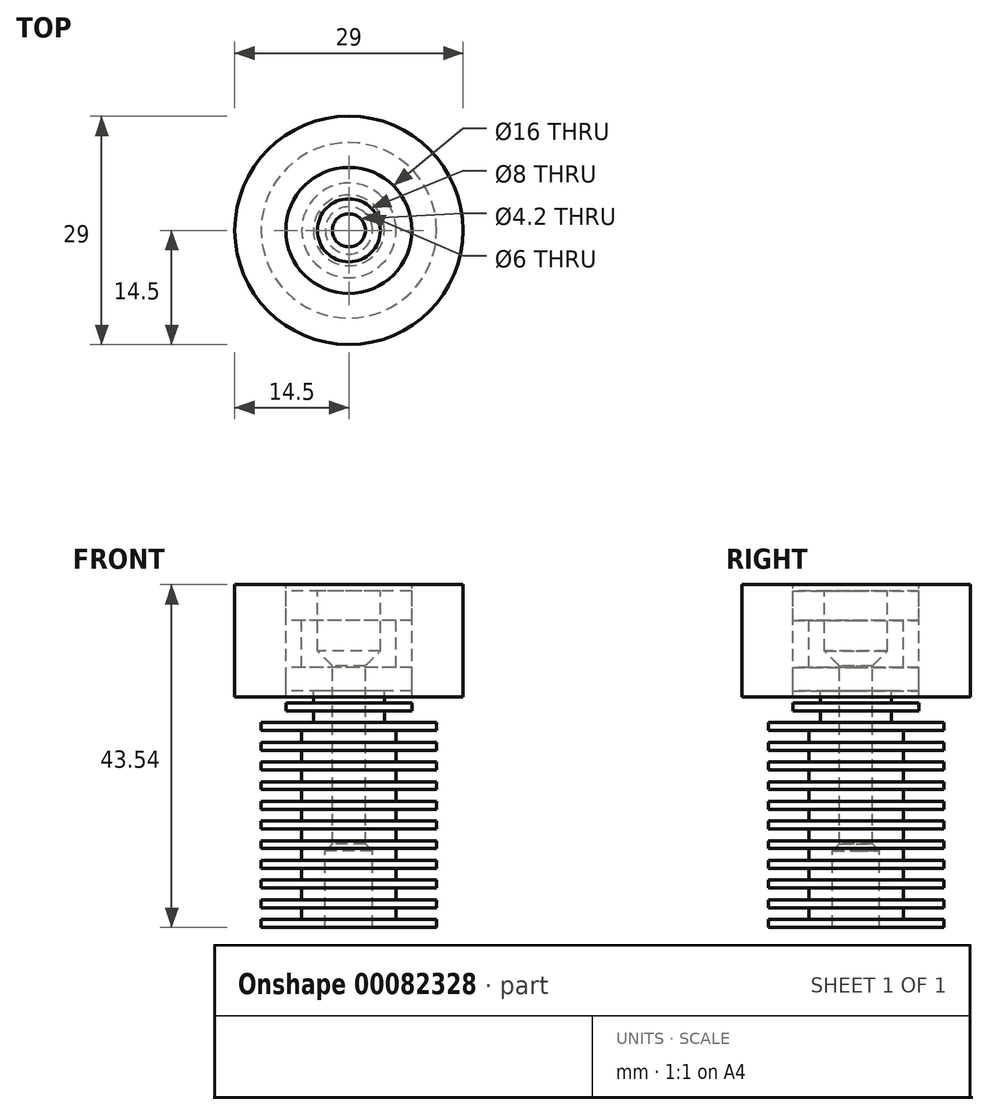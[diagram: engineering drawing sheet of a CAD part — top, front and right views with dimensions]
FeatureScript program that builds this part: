
annotation { "Feature Type Name" : "Feature", "Feature Type Description" : "" }
export const myFeature = defineFeature(function(context is Context, id is Id, definition is map)
    precondition{}
    {
        {
            var Q0;
            Q0=qCreatedBy(makeId("Front.planeOp"),FACE);
            var sketch = newSketch(context, id + "F0", { "sketchPlane" : qUnion([Q0])});
            skLineSegment(sketch, "E0", {"start": v(-11.15, 0) * mm, "end": v(-11.15, 1) * mm});
            skLineSegment(sketch, "E1", {"start": v(-11.15, 1) * mm, "end": v(-6, 1) * mm});
            skLineSegment(sketch, "E2", {"start": v(-6, 1) * mm, "end": v(-6, 2.5) * mm});
            skLineSegment(sketch, "E3", {"start": v(-6, 2.5) * mm, "end": v(-11.15, 2.5) * mm});
            skLineSegment(sketch, "E4.0.1.0", {"start": v(-11.15, 2.5) * mm, "end": v(-11.15, 3.5) * mm});
            skLineSegment(sketch, "E4.0.1.1", {"start": v(-11.15, 3.5) * mm, "end": v(-6, 3.5) * mm});
            skLineSegment(sketch, "E4.0.1.2", {"start": v(-6, 3.5) * mm, "end": v(-6, 5) * mm});
            skLineSegment(sketch, "E4.0.1.3", {"start": v(-6, 5) * mm, "end": v(-11.15, 5) * mm});
            skLineSegment(sketch, "E4.0.2.0", {"start": v(-11.15, 5) * mm, "end": v(-11.15, 6) * mm});
            skLineSegment(sketch, "E4.0.2.1", {"start": v(-11.15, 6) * mm, "end": v(-6, 6) * mm});
            skLineSegment(sketch, "E4.0.2.2", {"start": v(-6, 6) * mm, "end": v(-6, 7.5) * mm});
            skLineSegment(sketch, "E4.0.2.3", {"start": v(-6, 7.5) * mm, "end": v(-11.15, 7.5) * mm});
            skLineSegment(sketch, "E4.0.3.0", {"start": v(-11.15, 7.5) * mm, "end": v(-11.15, 8.5) * mm});
            skLineSegment(sketch, "E4.0.3.1", {"start": v(-11.15, 8.5) * mm, "end": v(-6, 8.5) * mm});
            skLineSegment(sketch, "E4.0.3.2", {"start": v(-6, 8.5) * mm, "end": v(-6, 10) * mm});
            skLineSegment(sketch, "E4.0.3.3", {"start": v(-6, 10) * mm, "end": v(-11.15, 10) * mm});
            skLineSegment(sketch, "E4.0.4.0", {"start": v(-11.15, 10) * mm, "end": v(-11.15, 11) * mm});
            skLineSegment(sketch, "E4.0.4.1", {"start": v(-11.15, 11) * mm, "end": v(-6, 11) * mm});
            skLineSegment(sketch, "E4.0.4.2", {"start": v(-6, 11) * mm, "end": v(-6, 12.5) * mm});
            skLineSegment(sketch, "E4.0.4.3", {"start": v(-6, 12.5) * mm, "end": v(-11.15, 12.5) * mm});
            skLineSegment(sketch, "E4.0.5.0", {"start": v(-11.15, 12.5) * mm, "end": v(-11.15, 13.5) * mm});
            skLineSegment(sketch, "E4.0.5.1", {"start": v(-11.15, 13.5) * mm, "end": v(-6, 13.5) * mm});
            skLineSegment(sketch, "E4.0.5.2", {"start": v(-6, 13.5) * mm, "end": v(-6, 15) * mm});
            skLineSegment(sketch, "E4.0.5.3", {"start": v(-6, 15) * mm, "end": v(-11.15, 15) * mm});
            skLineSegment(sketch, "E4.0.6.0", {"start": v(-11.15, 15) * mm, "end": v(-11.15, 16) * mm});
            skLineSegment(sketch, "E4.0.6.1", {"start": v(-11.15, 16) * mm, "end": v(-6, 16) * mm});
            skLineSegment(sketch, "E4.0.6.2", {"start": v(-6, 16) * mm, "end": v(-6, 17.5) * mm});
            skLineSegment(sketch, "E4.0.6.3", {"start": v(-6, 17.5) * mm, "end": v(-11.15, 17.5) * mm});
            skLineSegment(sketch, "E4.0.7.0", {"start": v(-11.15, 17.5) * mm, "end": v(-11.15, 18.5) * mm});
            skLineSegment(sketch, "E4.0.7.1", {"start": v(-11.15, 18.5) * mm, "end": v(-6, 18.5) * mm});
            skLineSegment(sketch, "E4.0.7.2", {"start": v(-6, 18.5) * mm, "end": v(-6, 20) * mm});
            skLineSegment(sketch, "E4.0.7.3", {"start": v(-6, 20) * mm, "end": v(-11.15, 20) * mm});
            skLineSegment(sketch, "E4.0.8.0", {"start": v(-11.15, 20) * mm, "end": v(-11.15, 21) * mm});
            skLineSegment(sketch, "E4.0.8.1", {"start": v(-11.15, 21) * mm, "end": v(-6, 21) * mm});
            skLineSegment(sketch, "E4.0.8.2", {"start": v(-6, 21) * mm, "end": v(-6, 22.5) * mm});
            skLineSegment(sketch, "E4.0.8.3", {"start": v(-6, 22.5) * mm, "end": v(-11.15, 22.5) * mm});
            skLineSegment(sketch, "E4.0.9.0", {"start": v(-11.15, 22.5) * mm, "end": v(-11.15, 23.5) * mm});
            skLineSegment(sketch, "E4.0.9.1", {"start": v(-11.15, 23.5) * mm, "end": v(-6, 23.5) * mm});
            skLineSegment(sketch, "E4.0.9.2", {"start": v(-6, 23.5) * mm, "end": v(-6, 25) * mm});
            skLineSegment(sketch, "E4.0.9.3", {"start": v(-6, 25) * mm, "end": v(-11.15, 25) * mm});
            skLineSegment(sketch, "E4.direction1", {"start": v(-11.15, 0) * mm, "end": v(19.55, 0) * mm, "construction": true});
            skLineSegment(sketch, "E4.direction2", {"start": v(-11.15, 0) * mm, "end": v(-11.15, 2.5) * mm, "construction": true});
            skLineSegment(sketch, "E5", {"start": v(-11.15, 25) * mm, "end": v(-11.15, 26) * mm});
            skLineSegment(sketch, "E6", {"start": v(-11.15, 26) * mm, "end": v(-4.5, 26) * mm});
            skLineSegment(sketch, "E7", {"start": v(-4.5, 26) * mm, "end": v(-4.5, 27.5) * mm});
            skLineSegment(sketch, "E8", {"start": v(-4.5, 27.5) * mm, "end": v(-8, 27.5) * mm});
            skLineSegment(sketch, "E9", {"start": v(-8, 27.5) * mm, "end": v(-8, 28.5) * mm});
            skLineSegment(sketch, "E10", {"start": v(-8, 28.5) * mm, "end": v(-4.5, 28.5) * mm});
            skLineSegment(sketch, "E11", {"start": v(-4.5, 28.5) * mm, "end": v(-4.5, 30) * mm});
            skLineSegment(sketch, "E12", {"start": v(-4.5, 30) * mm, "end": v(-8, 30) * mm});
            skLineSegment(sketch, "E13", {"start": v(-8, 30) * mm, "end": v(-8, 33) * mm});
            skLineSegment(sketch, "E14", {"start": v(-8, 33) * mm, "end": v(-6, 33) * mm});
            skLineSegment(sketch, "E15", {"start": v(-6, 33) * mm, "end": v(-6, 39) * mm});
            skLineSegment(sketch, "E16", {"start": v(-6, 39) * mm, "end": v(-8, 39) * mm});
            skLineSegment(sketch, "E17", {"start": v(-8, 39) * mm, "end": v(-8, 42.7) * mm});
            skLineSegment(sketch, "E18", {"start": v(-8, 42.7) * mm, "end": v(-4, 42.7) * mm});
            skLineSegment(sketch, "E19", {"start": v(-4, 42.7) * mm, "end": v(-4, 35.12) * mm});
            skLineSegment(sketch, "E20", {"start": v(-4, 35.12) * mm, "end": v(-2.1, 33.22) * mm});
            skLineSegment(sketch, "E21", {"start": v(-2.1, 33.22) * mm, "end": v(-2.1, 10.62) * mm});
            skLineSegment(sketch, "E22", {"start": v(-2.1, 10.62) * mm, "end": v(-3, 9.72) * mm});
            skLineSegment(sketch, "E23", {"start": v(-3, 9.72) * mm, "end": v(-3, 0) * mm});
            skLineSegment(sketch, "E24", {"start": v(-3, 0) * mm, "end": v(-11.15, 0) * mm});
            skLineSegment(sketch, "E25.MirrorCS", {"start": v(11.15, 25) * mm, "end": v(11.15, 26) * mm});
            skLineSegment(sketch, "E26.MirrorCS", {"start": v(2.1, 10.62) * mm, "end": v(3, 9.72) * mm});
            skLineSegment(sketch, "E27.MirrorCS", {"start": v(11.15, 12.5) * mm, "end": v(11.15, 13.5) * mm});
            skLineSegment(sketch, "E28.MirrorCS", {"start": v(11.15, 22.5) * mm, "end": v(11.15, 23.5) * mm});
            skLineSegment(sketch, "E29.MirrorCS", {"start": v(11.15, 17.5) * mm, "end": v(11.15, 18.5) * mm});
            skLineSegment(sketch, "E30.MirrorCS", {"start": v(8, 27.5) * mm, "end": v(8, 28.5) * mm});
            skLineSegment(sketch, "E31.MirrorCS", {"start": v(11.15, 20) * mm, "end": v(11.15, 21) * mm});
            skLineSegment(sketch, "E32.MirrorCS", {"start": v(11.15, 0) * mm, "end": v(11.15, 1) * mm});
            skLineSegment(sketch, "E33.MirrorCS", {"start": v(11.15, 7.5) * mm, "end": v(11.15, 8.5) * mm});
            skLineSegment(sketch, "E34.MirrorCS", {"start": v(11.15, 2.5) * mm, "end": v(11.15, 3.5) * mm});
            skLineSegment(sketch, "E35.MirrorCS", {"start": v(11.15, 10) * mm, "end": v(11.15, 11) * mm});
            skLineSegment(sketch, "E36.MirrorCS", {"start": v(11.15, 15) * mm, "end": v(11.15, 16) * mm});
            skLineSegment(sketch, "E37.MirrorCS", {"start": v(11.15, 5) * mm, "end": v(11.15, 6) * mm});
            skLineSegment(sketch, "E38.MirrorCS", {"start": v(2.1, 33.22) * mm, "end": v(2.1, 10.62) * mm});
            skLineSegment(sketch, "E39.MirrorCS", {"start": v(6, 16) * mm, "end": v(6, 17.5) * mm});
            skLineSegment(sketch, "E40.MirrorCS", {"start": v(6, 12.5) * mm, "end": v(11.15, 12.5) * mm});
            skLineSegment(sketch, "E41.MirrorCS", {"start": v(8, 33) * mm, "end": v(6, 33) * mm});
            skLineSegment(sketch, "E42.MirrorCS", {"start": v(6, 22.5) * mm, "end": v(11.15, 22.5) * mm});
            skLineSegment(sketch, "E43.MirrorCS", {"start": v(11.15, 26) * mm, "end": v(4.5, 26) * mm});
            skLineSegment(sketch, "E44.MirrorCS", {"start": v(6, 17.5) * mm, "end": v(11.15, 17.5) * mm});
            skLineSegment(sketch, "E45.MirrorCS", {"start": v(3, 0) * mm, "end": v(11.15, 0) * mm});
            skLineSegment(sketch, "E46.MirrorCS", {"start": v(4.5, 27.5) * mm, "end": v(8, 27.5) * mm});
            skLineSegment(sketch, "E47.MirrorCS", {"start": v(6, 33) * mm, "end": v(6, 39) * mm});
            skLineSegment(sketch, "E48.MirrorCS", {"start": v(11.15, 18.5) * mm, "end": v(6, 18.5) * mm});
            skLineSegment(sketch, "E49.MirrorCS", {"start": v(3, 9.72) * mm, "end": v(3, 0) * mm});
            skLineSegment(sketch, "E50.MirrorCS", {"start": v(4.5, 26) * mm, "end": v(4.5, 27.5) * mm});
            skLineSegment(sketch, "E51.MirrorCS", {"start": v(11.15, 13.5) * mm, "end": v(6, 13.5) * mm});
            skLineSegment(sketch, "E52.MirrorCS", {"start": v(6, 39) * mm, "end": v(8, 39) * mm});
            skLineSegment(sketch, "E53.MirrorCS", {"start": v(11.15, 23.5) * mm, "end": v(6, 23.5) * mm});
            skLineSegment(sketch, "E54.MirrorCS", {"start": v(6, 18.5) * mm, "end": v(6, 20) * mm});
            skLineSegment(sketch, "E55.MirrorCS", {"start": v(6, 13.5) * mm, "end": v(6, 15) * mm});
            skLineSegment(sketch, "E56.MirrorCS", {"start": v(8, 28.5) * mm, "end": v(4.5, 28.5) * mm});
            skLineSegment(sketch, "E57.MirrorCS", {"start": v(8, 39) * mm, "end": v(8, 42.7) * mm});
            skLineSegment(sketch, "E58.MirrorCS", {"start": v(6, 20) * mm, "end": v(11.15, 20) * mm});
            skLineSegment(sketch, "E59.MirrorCS", {"start": v(6, 23.5) * mm, "end": v(6, 25) * mm});
            skLineSegment(sketch, "E60.MirrorCS", {"start": v(11.15, 8.5) * mm, "end": v(6, 8.5) * mm});
            skLineSegment(sketch, "E61.MirrorCS", {"start": v(4.5, 28.5) * mm, "end": v(4.5, 30) * mm});
            skLineSegment(sketch, "E62.MirrorCS", {"start": v(6, 8.5) * mm, "end": v(6, 10) * mm});
            skLineSegment(sketch, "E63.MirrorCS", {"start": v(6, 10) * mm, "end": v(11.15, 10) * mm});
            skLineSegment(sketch, "E64.MirrorCS", {"start": v(6, 21) * mm, "end": v(6, 22.5) * mm});
            skLineSegment(sketch, "E65.MirrorCS", {"start": v(8, 30) * mm, "end": v(8, 33) * mm});
            skLineSegment(sketch, "E66.MirrorCS", {"start": v(4, 35.12) * mm, "end": v(2.1, 33.22) * mm});
            skLineSegment(sketch, "E67.MirrorCS", {"start": v(6, 7.5) * mm, "end": v(11.15, 7.5) * mm});
            skLineSegment(sketch, "E68.MirrorCS", {"start": v(6, 6) * mm, "end": v(6, 7.5) * mm});
            skLineSegment(sketch, "E69.MirrorCS", {"start": v(11.15, 16) * mm, "end": v(6, 16) * mm});
            skLineSegment(sketch, "E70.MirrorCS", {"start": v(11.15, 0) * mm, "end": v(11.15, 2.5) * mm, "construction": true});
            skLineSegment(sketch, "E71.MirrorCS", {"start": v(6, 25) * mm, "end": v(11.15, 25) * mm});
            skLineSegment(sketch, "E72.MirrorCS", {"start": v(11.15, 1) * mm, "end": v(6, 1) * mm});
            skLineSegment(sketch, "E73.MirrorCS", {"start": v(8, 42.7) * mm, "end": v(4, 42.7) * mm});
            skLineSegment(sketch, "E74.MirrorCS", {"start": v(6, 15) * mm, "end": v(11.15, 15) * mm});
            skLineSegment(sketch, "E75.MirrorCS", {"start": v(6, 1) * mm, "end": v(6, 2.5) * mm});
            skLineSegment(sketch, "E76.MirrorCS", {"start": v(6, 2.5) * mm, "end": v(11.15, 2.5) * mm});
            skLineSegment(sketch, "E77.MirrorCS", {"start": v(6, 11) * mm, "end": v(6, 12.5) * mm});
            skLineSegment(sketch, "E78.MirrorCS", {"start": v(11.15, 3.5) * mm, "end": v(6, 3.5) * mm});
            skLineSegment(sketch, "E79.MirrorCS", {"start": v(6, 5) * mm, "end": v(11.15, 5) * mm});
            skLineSegment(sketch, "E80.MirrorCS", {"start": v(11.15, 6) * mm, "end": v(6, 6) * mm});
            skLineSegment(sketch, "E81.MirrorCS", {"start": v(4, 42.7) * mm, "end": v(4, 35.12) * mm});
            skLineSegment(sketch, "E82.MirrorCS", {"start": v(11.15, 11) * mm, "end": v(6, 11) * mm});
            skLineSegment(sketch, "E83.MirrorCS", {"start": v(11.15, 21) * mm, "end": v(6, 21) * mm});
            skLineSegment(sketch, "E84.MirrorCS", {"start": v(4.5, 30) * mm, "end": v(8, 30) * mm});
            skLineSegment(sketch, "E85.MirrorCS", {"start": v(6, 3.5) * mm, "end": v(6, 5) * mm});
            skLineSegment(sketch, "E86", {"start": v(0, 42.7) * mm, "end": v(0, 0) * mm, "construction": true});
            skLineSegment(sketch, "E87.bottom", {"start": v(-8, 43.54) * mm, "end": v(-14.5, 43.54) * mm});
            skLineSegment(sketch, "E87.top", {"start": v(-8, 29.23) * mm, "end": v(-14.5, 29.23) * mm});
            skLineSegment(sketch, "E87.left", {"start": v(-8, 43.54) * mm, "end": v(-8, 29.23) * mm});
            skLineSegment(sketch, "E87.right", {"start": v(-14.5, 43.54) * mm, "end": v(-14.5, 29.23) * mm});
            skLineSegment(sketch, "E88.MirrorCS", {"start": v(8, 43.54) * mm, "end": v(8, 29.23) * mm});
            skLineSegment(sketch, "E89.MirrorCS", {"start": v(8, 43.54) * mm, "end": v(14.5, 43.54) * mm});
            skLineSegment(sketch, "E90.MirrorCS", {"start": v(14.5, 43.54) * mm, "end": v(14.5, 29.23) * mm});
            skLineSegment(sketch, "E91.MirrorCS", {"start": v(8, 29.23) * mm, "end": v(14.5, 29.23) * mm});
            skSolve(sketch);
        }
        {
            var Q0;
            Q0=makeQuery(id+"F0.imprint","IMPRINT",FACE,{"disambiguationData":[TD([[makeQuery(id+"F0.imprint","IMPRINT",EDGE,{"derivedFrom":sQuery(id+"F0.wireOp",EDGE,"E25.MirrorCS")}),1.0]])]});
            var Q1;
            Q1=sQuery(id+"F0.wireOp",EDGE,"E86");
            revolve(context, id + "F1", {"entities" : qUnion([Q0]), "axis" : qUnion([Q1]), "revolveType" : RevolveType.FULL});
        }
        {
            var Q0;
            {var subQ3=sQuery(id+"F0.wireOp",EDGE,"E87.bottom");Q0=makeQuery(id+"F0.imprint","IMPRINT",FACE,{"disambiguationData":[TD([[makeQuery(id+"F0.imprint","IMPRINT",EDGE,{"derivedFrom":subQ3}),1.0]])]});}
            var Q1;
            Q1=sQuery(id+"F0.wireOp",EDGE,"E86");
            revolve(context, id + "F2", {"entities" : qUnion([Q0]), "axis" : qUnion([Q1]), "revolveType" : RevolveType.FULL});
        }
    });
